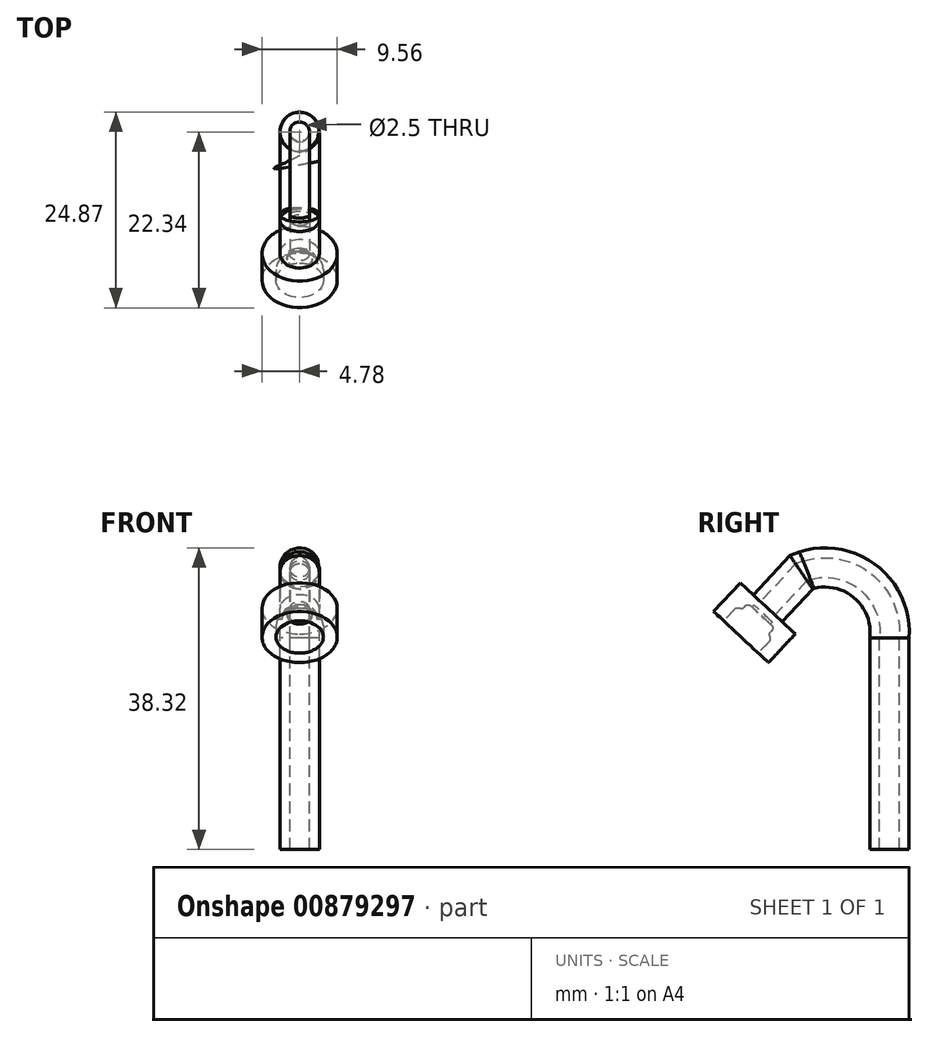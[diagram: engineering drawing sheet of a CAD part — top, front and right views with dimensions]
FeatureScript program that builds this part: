
annotation { "Feature Type Name" : "Feature", "Feature Type Description" : "" }
export const myFeature = defineFeature(function(context is Context, id is Id, definition is map)
    precondition{}
    {
        {
            var Q0;
            Q0=qCreatedBy(makeId("Top.planeOp"),FACE);
            var sketch = newSketch(context, id + "F0", { "sketchPlane" : qUnion([Q0])});
            skCircle(sketch, "E0", {"center": v(0, 0) * mm, "radius": 2.5 * mm});
            skCircle(sketch, "E1", {"center": v(0, 0) * mm, "radius": 1.25 * mm});
            skSolve(sketch);
        }
        {
            var Q0;
            Q0=qCreatedBy(makeId("Right.planeOp"),FACE);
            var sketch = newSketch(context, id + "F1", { "sketchPlane" : qUnion([Q0])});
            skLineSegment(sketch, "E2", {"start": v(0, 0.75) * mm, "end": v(0, 27.62) * mm});
            skArc(sketch, "E3", {"start": v(0, 27.62) * mm, "mid": v(-3.58, 34.38) * mm, "end": v(-11.2, 35.22) * mm});
            skLineSegment(sketch, "E4", {"start": v(-11.2, 35.22) * mm, "end": v(-15.97, 30.1) * mm});
            skSolve(sketch);
        }
        {
            var Q0;
            Q0=makeQuery(id+"F0.imprint","IMPRINT",FACE,{"disambiguationData":[TD([[makeQuery(id+"F0.imprint","IMPRINT",EDGE,{"derivedFrom":sQuery(id+"F0.wireOp",EDGE,"E0")}),1.0]])]});
            var Q1;
            Q1=sQuery(id+"F1.wireOp",EDGE,"E2");
            var Q2;
            Q2=sQuery(id+"F1.wireOp",EDGE,"E3");
            var Q3;
            Q3=sQuery(id+"F1.wireOp",EDGE,"E4");
            sweep(context, id + "F2", {"profiles" : qUnion([Q0]), "path" : qUnion([Q1, Q2, Q3])});
        }
        {
            var Q0;
            Q0=qCreatedBy(makeId("Right.planeOp"),FACE);
            var sketch = newSketch(context, id + "F3", { "sketchPlane" : qUnion([Q0])});
            skLineSegment(sketch, "E5.0", {"start": v(-13.63, 28.94) * mm, "end": v(-17.29, 32.35) * mm});
            skLineSegment(sketch, "E6", {"start": v(-16.64, 24.95) * mm, "end": v(-15.3, 26.4) * mm});
            skLineSegment(sketch, "E7", {"start": v(-15.17, 26.84) * mm, "end": v(-15.24, 27.18) * mm});
            skLineSegment(sketch, "E8", {"start": v(-15.12, 27.62) * mm, "end": v(-14.95, 27.8) * mm});
            skLineSegment(sketch, "E9", {"start": v(-14.98, 28.5) * mm, "end": v(-15.13, 28.64) * mm});
            skPoint(sketch, "E10.visualSharp", {"position": v(-15.12, 26.59) * mm});
            skArc(sketch, "E10.filletArc", {"start": v(-15.3, 26.4) * mm, "mid": v(-15.18, 26.6) * mm, "end": v(-15.17, 26.84) * mm});
            skPoint(sketch, "E11.visualSharp", {"position": v(-15.3, 27.43) * mm});
            skArc(sketch, "E11.filletArc", {"start": v(-15.12, 27.62) * mm, "mid": v(-15.23, 27.41) * mm, "end": v(-15.24, 27.18) * mm});
            skPoint(sketch, "E12.visualSharp", {"position": v(-14.61, 28.16) * mm});
            skArc(sketch, "E12.filletArc", {"start": v(-14.95, 27.8) * mm, "mid": v(-14.82, 28.15) * mm, "end": v(-14.98, 28.5) * mm});
            skLineSegment(sketch, "E13", {"start": v(-16.64, 24.95) * mm, "end": v(-15.35, 23.75) * mm});
            skLineSegment(sketch, "E14", {"start": v(-15.35, 23.75) * mm, "end": v(-11.96, 27.39) * mm});
            skLineSegment(sketch, "E15", {"start": v(-11.96, 27.39) * mm, "end": v(-14.29, 29.55) * mm});
            skLineSegment(sketch, "E16", {"start": v(-14.29, 29.55) * mm, "end": v(-15.13, 28.64) * mm});
            skLineSegment(sketch, "E17", {"start": v(-14.89, 28.9) * mm, "end": v(-13.94, 28.02) * mm});
            skLineSegment(sketch, "E18", {"start": v(-13.94, 28.02) * mm, "end": v(-13.33, 28.67) * mm});
            skLineSegment(sketch, "E19", {"start": v(-13.94, 28.02) * mm, "end": v(-13.72, 27.82) * mm});
            skLineSegment(sketch, "E20", {"start": v(-13.72, 27.82) * mm, "end": v(-13.11, 28.46) * mm});
            skLineSegment(sketch, "E21.MirrorCS", {"start": v(-15.84, 29.8) * mm, "end": v(-15.24, 30.44) * mm});
            skLineSegment(sketch, "E22.MirrorCS", {"start": v(-15.84, 29.8) * mm, "end": v(-16.06, 30) * mm});
            skPoint(sketch, "E23.MirrorP", {"position": v(-15.65, 29.13) * mm});
            skLineSegment(sketch, "E24.MirrorCS", {"start": v(-14.89, 28.9) * mm, "end": v(-15.84, 29.8) * mm});
            skLineSegment(sketch, "E25.MirrorCS", {"start": v(-16.06, 30) * mm, "end": v(-15.46, 30.64) * mm});
            skLineSegment(sketch, "E26", {"start": v(-15.46, 30.64) * mm, "end": v(-14.29, 29.55) * mm});
            skLineSegment(sketch, "E27.0", {"start": v(-14.61, 28.16) * mm, "end": v(-15.13, 28.64) * mm, "construction": true});
            skLineSegment(sketch, "E27.1", {"start": v(-14.61, 28.16) * mm, "end": v(-15.3, 27.43) * mm, "construction": true});
            skLineSegment(sketch, "E27.8", {"start": v(-14.1, 27.69) * mm, "end": v(-15.13, 28.64) * mm, "construction": true});
            skLineSegment(sketch, "E27.9", {"start": v(-14.1, 27.69) * mm, "end": v(-15.12, 26.59) * mm, "construction": true});
            skPoint(sketch, "E28", {"position": v(-15.46, 30.64) * mm});
            skSolve(sketch);
        }
        {
            var Q0;
            {var subQ0=sQuery(id+"F3.wireOp",EDGE,"E21.MirrorCS");Q0=makeQuery(id+"F3.imprint","IMPRINT",FACE,{"disambiguationData":[TD([[makeQuery(id+"F3.imprint","IMPRINT",EDGE,{"derivedFrom":subQ0}),1.0]])]});}
            var Q1;
            Q1=makeQuery(id+"F3.imprint","IMPRINT",FACE,{"disambiguationData":[TD([[makeQuery(id+"F3.imprint","IMPRINT",EDGE,{"derivedFrom":sQuery(id+"F3.wireOp",EDGE,"E6")}),-1.0]])]});
            var Q2;
            {var subQ0=sQuery(id+"F3.wireOp",EDGE,"E18");Q2=makeQuery(id+"F3.imprint","IMPRINT",FACE,{"disambiguationData":[TD([[makeQuery(id+"F3.imprint","IMPRINT",EDGE,{"derivedFrom":subQ0}),-1.0]])]});}
            var Q3;
            {var subQ4=sQuery(id+"F3.wireOp",EDGE,"E21.MirrorCS");Q3=makeQuery(id+"F3.imprint","IMPRINT",FACE,{"disambiguationData":[TD([[makeQuery(id+"F3.imprint","IMPRINT",EDGE,{"derivedFrom":subQ4}),-1.0]])]});}
            var Q4;
            {var subQ4=sQuery(id+"F3.wireOp",EDGE,"E17");Q4=makeQuery(id+"F3.imprint","IMPRINT",FACE,{"disambiguationData":[TD([[makeQuery(id+"F3.imprint","IMPRINT",EDGE,{"derivedFrom":subQ4}),1.0]])]});}
            var Q5;
            Q5=sQuery(id+"F3.wireOp",EDGE,"E25.MirrorCS");
            revolve(context, id + "F4", {"operationType" : NewBodyOperationType.ADD, "surfaceOperationType" : NewSurfaceOperationType.NEW, "entities" : qUnion([Q0, Q1, Q2, Q3, Q4]), "axis" : qUnion([Q5]), "revolveType" : RevolveType.FULL});
        }
    });
